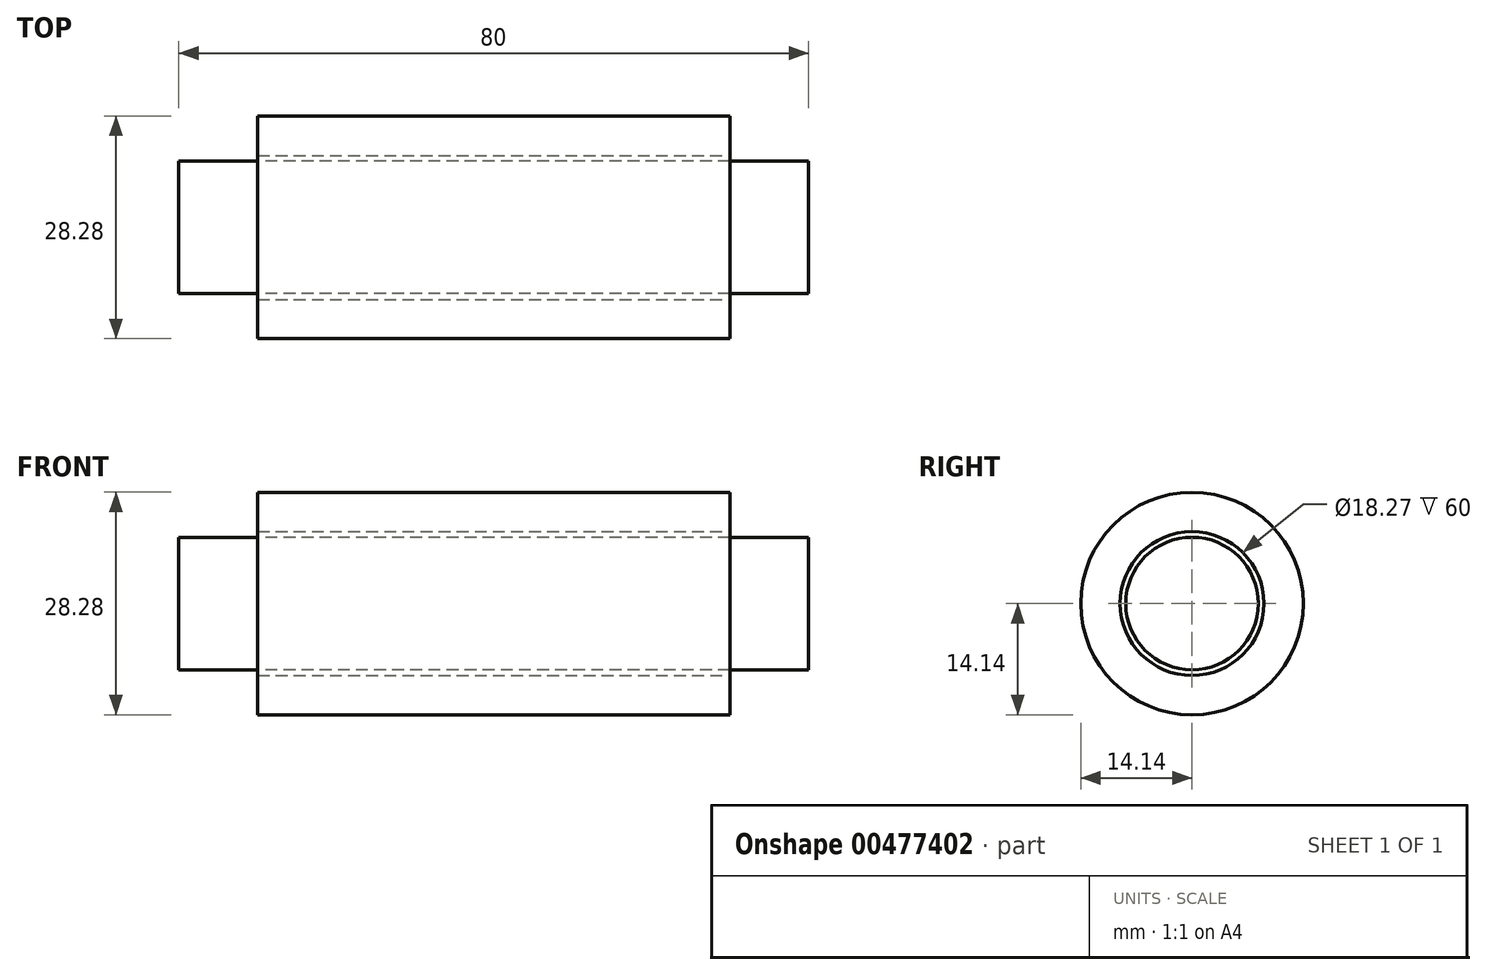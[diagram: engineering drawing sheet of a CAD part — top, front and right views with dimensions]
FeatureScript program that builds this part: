
annotation { "Feature Type Name" : "Feature", "Feature Type Description" : "" }
export const myFeature = defineFeature(function(context is Context, id is Id, definition is map)
    precondition{}
    {
        {
            var Q0;
            Q0=qCreatedBy(makeId("Right.planeOp"),FACE);
            var sketch = newSketch(context, id + "F0", { "sketchPlane" : qUnion([Q0])});
            skCircle(sketch, "E0", {"center": v(0, 0) * mm, "radius": 8.42 * mm});
            skSolve(sketch);
        }
        {
            var Q0;
            Q0=makeQuery(id+"F0.imprint","IMPRINT",FACE,{"disambiguationData":[TD([[makeQuery(id+"F0.imprint","IMPRINT",EDGE,{"derivedFrom":sQuery(id+"F0.wireOp",EDGE,"E0")}),1.0]])]});
            extrude(context, id + "F1", {"entities" : qUnion([Q0]), "depth" : 80 * mm, "offsetDistance" : 25 * mm, "symmetric" : true});
        }
        {
            var Q0;
            Q0=qCreatedBy(makeId("Front.planeOp"),FACE);
            var sketch = newSketch(context, id + "F2", { "sketchPlane" : qUnion([Q0])});
            skLineSegment(sketch, "E1.bottom", {"start": v(-30, 9.14) * mm, "end": v(30, 9.14) * mm});
            skLineSegment(sketch, "E1.top", {"start": v(-30, 14.14) * mm, "end": v(30, 14.14) * mm});
            skLineSegment(sketch, "E1.left", {"start": v(-30, 9.14) * mm, "end": v(-30, 14.14) * mm});
            skLineSegment(sketch, "E1.right", {"start": v(30, 9.14) * mm, "end": v(30, 14.14) * mm});
            skLineSegment(sketch, "E2.bottom", {"start": v(-22, 14.14) * mm, "end": v(22, 14.14) * mm});
            skLineSegment(sketch, "E2.top", {"start": v(-22, 20.3) * mm, "end": v(22, 20.3) * mm});
            skLineSegment(sketch, "E2.left", {"start": v(-22, 14.14) * mm, "end": v(-22, 20.3) * mm});
            skLineSegment(sketch, "E2.right", {"start": v(22, 14.14) * mm, "end": v(22, 20.3) * mm});
            skLineSegment(sketch, "E3.bottom", {"start": v(-22, 20.3) * mm, "end": v(-17, 20.3) * mm});
            skLineSegment(sketch, "E3.top", {"start": v(-22, 38.3) * mm, "end": v(-17, 38.3) * mm});
            skLineSegment(sketch, "E3.left", {"start": v(-22, 20.3) * mm, "end": v(-22, 38.3) * mm});
            skLineSegment(sketch, "E3.right", {"start": v(-17, 20.3) * mm, "end": v(-17, 38.3) * mm});
            skLineSegment(sketch, "E4.bottom", {"start": v(22, 20.3) * mm, "end": v(17, 20.3) * mm});
            skLineSegment(sketch, "E4.top", {"start": v(22, 38.3) * mm, "end": v(17, 38.3) * mm});
            skLineSegment(sketch, "E4.left", {"start": v(22, 20.3) * mm, "end": v(22, 38.3) * mm});
            skLineSegment(sketch, "E4.right", {"start": v(17, 20.3) * mm, "end": v(17, 38.3) * mm});
            skSolve(sketch);
        }
        {
            var Q0;
            Q0=makeQuery(id+"F2.imprint","IMPRINT",FACE,{"disambiguationData":[TD([[makeQuery(id+"F2.imprint","IMPRINT",EDGE,{"derivedFrom":sQuery(id+"F2.wireOp",EDGE,"E1.bottom")}),1.0]])]});
            var Q1;
            Q1=makeQuery(id+"F2.imprint","IMPRINT",FACE,{"disambiguationData":[TD([[makeQuery(id+"F2.imprint","IMPRINT",EDGE,{"derivedFrom":sQuery(id+"F2.wireOp",EDGE,"E2.bottom")}),1.0]])]});
            var Q2;
            Q2=makeQuery(id+"F2.imprint","IMPRINT",FACE,{"disambiguationData":[TD([[makeQuery(id+"F2.imprint","IMPRINT",EDGE,{"derivedFrom":sQuery(id+"F2.wireOp",EDGE,"E3.bottom")}),1.0]])]});
            var Q3;
            Q3=makeQuery(id+"F2.imprint","IMPRINT",FACE,{"disambiguationData":[TD([[makeQuery(id+"F2.imprint","IMPRINT",EDGE,{"derivedFrom":sQuery(id+"F2.wireOp",EDGE,"E4.bottom")}),-1.0]])]});
            var Q4;
            Q4=makeQuery(id+"F1.opExtrude","SWEPT_FACE",FACE,{"disambiguationData":[OSD([sQuery(id+"F0.wireOp",EDGE,"E0")])]});
            revolve(context, id + "F3", {"entities" : qUnion([Q0, Q1, Q2, Q3]), "axis" : qUnion([Q4]), "revolveType" : RevolveType.FULL});
        }
    });
